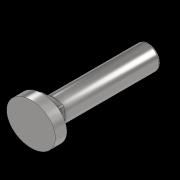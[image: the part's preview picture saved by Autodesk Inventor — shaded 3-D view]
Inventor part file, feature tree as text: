
AUTODESK INVENTOR PART (.ipt)
format: ipt  version: 2022.2 (Build 262287010, 287A)  size: 147,968 bytes
history: native  units: mm
features: extrude x3, sketch x3, fillet x2, thread x1
ambient origin geometry x8: Origin, YZ Plane, XZ Plane, XY Plane, X Axis, Y Axis, Z Axis, Center Point
bodies: Solid1 (feature_tree)
feature tree (9):
  extrude  "Extrusion1"  Depth=4.8mm
  extrude  "Extrusion2"  Depth=25.5mm
  extrude  "Extrusion3"  Depth=25.5mm TaperAngle=0.0deg
  fillet  "Fillet1"  Radius=5.45mm
  fillet  "Fillet2"  Radius=6.4mm
  thread  "Thread1"  [1 undecoded]
  sketch  "Sketch1"  dims[d0=6.2mm d1=4.8mm]
  sketch  "Sketch2"  dims[d2=25.5mm d3=0.0mm d4=6.35mm]
  sketch  "Sketch3"  dims[d5=6.35mm d6=2.5mm d7=0.0mm d8=5.45mm d9=6.4mm d10=3.0mm d11=0.0mm d12=0.5mm d13=0.5mm d14=25.5mm d15=0.0mm]
note: 1 required parameter value undecoded (feature->parameter linkage not recoverable at this tier; creation-order binding heuristic only, values carry confidence <= 0.55)
